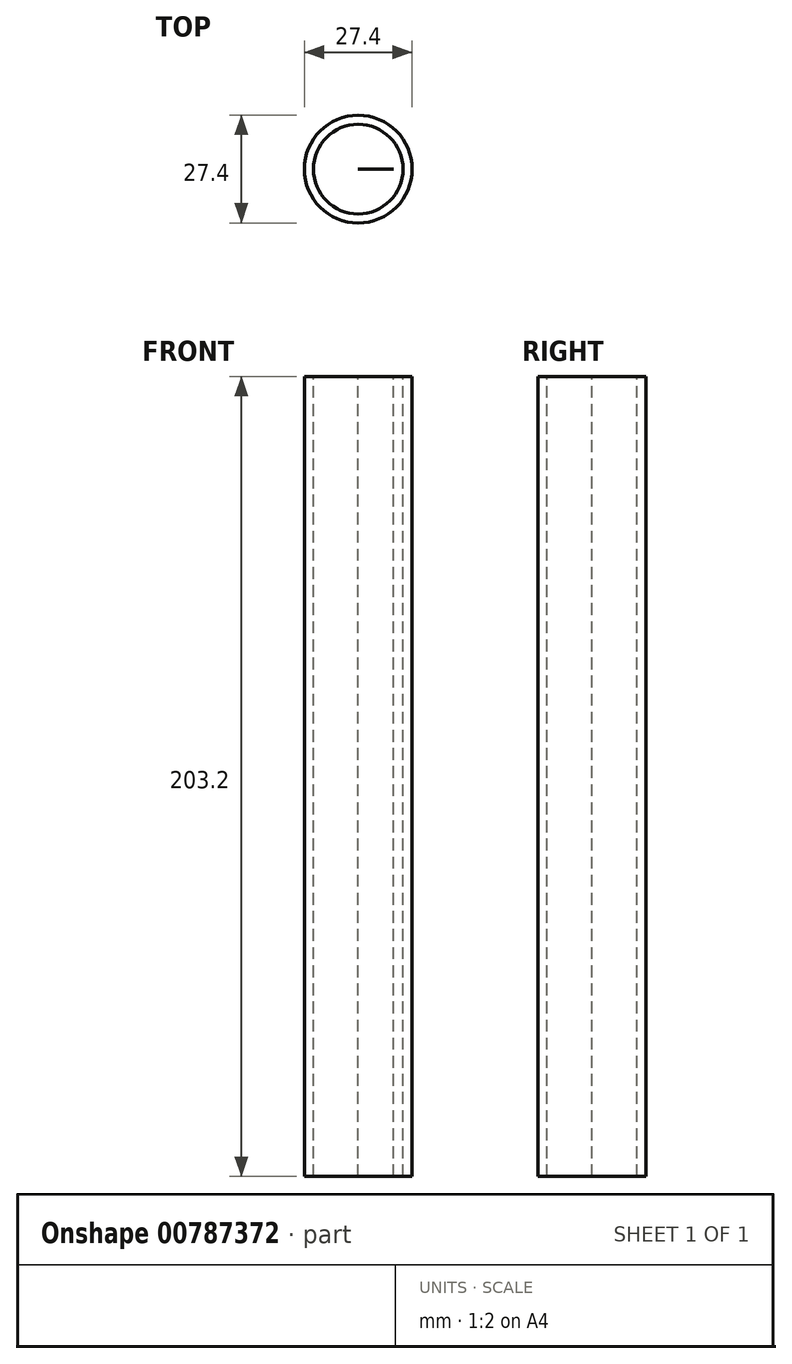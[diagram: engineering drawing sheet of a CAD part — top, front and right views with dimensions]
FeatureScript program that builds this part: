
annotation { "Feature Type Name" : "Feature", "Feature Type Description" : "" }
export const myFeature = defineFeature(function(context is Context, id is Id, definition is map)
    precondition{}
    {
        {
            var Q0;
            Q0=qCreatedBy(makeId("Top.planeOp"),FACE);
            var sketch = newSketch(context, id + "F0", { "sketchPlane" : qUnion([Q0])});
            skCircle(sketch, "E0", {"center": v(0, 0) * mm, "radius": 11.38 * mm});
            skCircle(sketch, "E1", {"center": v(0, 0) * mm, "radius": 13.7 * mm});
            skLineSegment(sketch, "E2", {"start": v(0, 0) * mm, "end": v(8.94, 0) * mm});
            skSolve(sketch);
        }
        {
            var Q0;
            Q0=sQuery(id+"F0.wireOp",EDGE,"E1");
            var Q1;
            Q1=sQuery(id+"F0.wireOp",EDGE,"E2");
            var Q2;
            Q2=sQuery(id+"F0.wireOp",EDGE,"E0");
            extrude(context, id + "F1", {"bodyType" : ToolBodyType.SURFACE, "surfaceEntities" : qUnion([Q0, Q1, Q2]), "depth" : 203.2 * mm, "offsetDistance" : 25.4 * mm});
        }
    });
